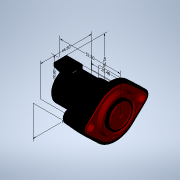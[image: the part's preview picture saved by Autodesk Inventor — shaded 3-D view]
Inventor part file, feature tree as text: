
AUTODESK INVENTOR PART (.ipt)
format: ipt  version: 2021 (Build 250183000, 183)  size: 797,696 bytes
history: native  units: mm
features: sketch x28, extrude x18, revolve x10, other x7, fillet x5, chamfer x1
ambient origin geometry x8: Origin, YZ Plane, XZ Plane, XY Plane, X Axis, Y Axis, Z Axis, Center Point
bodies: Solid1 (feature_tree)
feature tree (69):
  other  "Annotations"
  revolve  "Revolution1"  Angle=360.0deg
  revolve  "Revolution2"  [1 undecoded]
  revolve  "Revolution3"  [1 undecoded]
  extrude  "Extrusion1"  TaperAngle=360.0deg  [1 undecoded]
  extrude  "Extrusion2"  Depth=2.5mm TaperAngle=0.0deg
  extrude  "Extrusion3"  Depth=0.85mm
  extrude  "Extrusion4"  Depth=5.5mm TaperAngle=0.0deg
  revolve  "Revolution4"  Angle=60.0deg
  extrude  "Extrusion5"  Depth=0.788mm
  extrude  "Extrusion6"  Depth=6.3mm TaperAngle=0.0deg
  fillet  "Fillet1"  [1 undecoded]
  fillet  "Fillet2"  [1 undecoded]
  fillet  "Fillet3"  Radius=4.0mm
  extrude  "Extrusion7"  Depth=2.3mm TaperAngle=0.0deg
  extrude  "Extrusion8"  TaperAngle=360.0deg  [1 undecoded]
  revolve  "Revolution5"  [1 undecoded]
  extrude  "Extrusion9"  Depth=0.639mm TaperAngle=0.0deg
  fillet  "Fillet4"  Radius=1.3mm
  revolve  "Revolution6"  [1 undecoded]
  extrude  "Extrusion10"  [1 undecoded]
  chamfer  "Chamfer1"  [1 undecoded]
  revolve  "Revolution7"  [1 undecoded]
  revolve  "Revolution8"  [1 undecoded]
  extrude  "Extrusion11"  [1 undecoded]
  extrude  "Extrusion12"  [1 undecoded]
  extrude  "Extrusion13"  [1 undecoded]
  extrude  "Extrusion14"  [1 undecoded]
  revolve  "Revolution9"  [1 undecoded]
  revolve  "Revolution10"  [1 undecoded]
  extrude  "Extrusion15"  [1 undecoded]
  extrude  "Extrusion16"  [1 undecoded]
  extrude  "Extrusion17"  [1 undecoded]
  extrude  "Extrusion18"  [1 undecoded]
  fillet  "Fillet5"  [1 undecoded]
  sketch  "Sketch_1"  dims[d0=360.0deg d1=360.0deg]
  sketch  "Sketch_16"  dims[d37=1.6mm d38=0.0mm d39=2.3mm d40=0.0mm]
  sketch  "Sketch_17"  dims[d41=0.5mm d42=0.0mm d43=360.0deg]
  sketch  "Sketch_2"  dims[d2=360.0deg d3=14.5mm d4=0.0mm]
  sketch  "Sketch_3"  dims[d5=24.0mm d6=0.0mm d7=15.0mm d8=0.0mm]
  sketch  "Sketch_6"  dims[d16=0.6mm d17=0.85mm]
  sketch  "Sketch_7"  dims[d18=0.5mm d19=5.5mm d20=0.0mm]
  sketch  "Sketch_4"  dims[d9=13.2mm d10=0.0mm d11=360.0deg]
  sketch  "Sketch_5"  dims[d12=8.0mm d13=0.0mm d14=2.5mm d15=0.0mm]
  sketch  "Sketch_8"  dims[d21=20.0mm d22=0.0mm d23=60.0deg]
  sketch  "Sketch_11"  dims[d27=360.0deg d28=6.3mm d29=0.0mm]
  sketch  "Sketch_18"  dims[d44=360.0deg d45=15.0mm d46=0.0mm]
  sketch  "Sketch_12"  dims[d30=1.5mm d31=1.5mm d32=45.0deg d33=360.0deg d34=360.0deg d35=4.0mm d36=0.0mm]
  sketch  "Sketch_19"  dims[d47=1.939mm d48=0.0mm d49=0.639mm d50=0.0mm d51=1.3mm d52=0.0mm]
  sketch  "Sketch_20"  dims[d53=1.0mm]
  sketch  "Sketch_21"  dims[d54=25.4mm d55=43.3mm d56=44.5mm d57=57.3mm d58=29.8mm d59=52.5mm]
  sketch  "Sketch_22"
  sketch  "Sketch_23"
  sketch  "Sketch_24"
  sketch  "Sketch_25"
  sketch  "Sketch_26"
  sketch  "Sketch_27"
  sketch  "Sketch_28"
  sketch  "Sketch_29"
  sketch  "Sketch_9"  dims[d24=20.0mm d25=0.0mm d26=0.788mm]
  sketch  "Sketch_30"
  sketch  "Sketch_32"
  sketch  "Sketch_33"
  other  "Linear Dimension 1"
  other  "Linear Dimension 2"
  other  "Linear Dimension 3"
  other  "Linear Dimension 4"
  other  "Linear Dimension 5"
  other  "Linear Dimension 6"
note: 23 required parameter values undecoded (feature->parameter linkage not recoverable at this tier; creation-order binding heuristic only, values carry confidence <= 0.55)